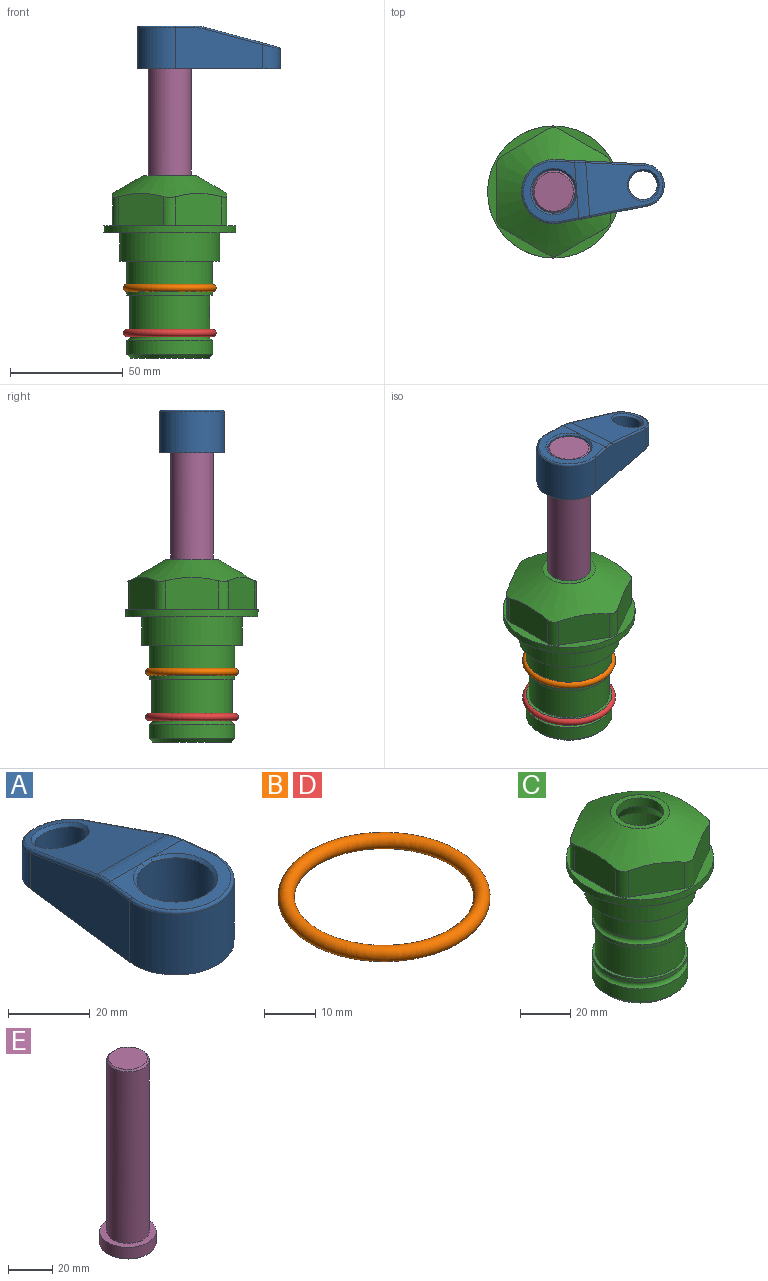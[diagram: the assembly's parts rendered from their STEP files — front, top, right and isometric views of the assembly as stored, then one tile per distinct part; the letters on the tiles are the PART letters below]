
ASSEMBLY  parts=5 mates=4
PART A: 31 faces, bbox 31.7x65.5x19.8 mm
  f0: plane 39.12x18.26mm, normal (0.99,0.12,0), area 612.2mm2, adj f1,f4,f7,f11,f13,f15
  f1: cylinder r=9.53mm len=18.91mm, axis (0,0,-1), area 296.1mm2, adj f0,f2,f7,f17
  f2: plane 39.12x18.26mm, normal (-0.99,0.12,0), area 612.2mm2, adj f1,f4,f7,f12,f14,f16
  f3: cylinder r=6.35mm len=12.7mm, axis (0,0,-1), area 362.4mm2, adj f7,f18
  f4: cylinder r=14.29mm len=28.58mm, axis (0,0,-1), area 882.2mm2, adj f0,f2,f7,f10
  f5: cylinder r=9.53mm len=19.05mm, axis (0,0,-1), area 1092.6mm2, adj f7,f19,f20
  f6: plane 26.99x23.69mm, normal (0,0,1), area 216.2mm2, adj f9,f10,f11,f12,f19
  f7: plane 63.5x28.58mm, normal (0,0,-1), area 661.8mm2, adj f0,f1,f2,f3,f4,f5,f22,f23
  f8: plane 33.52x23.6mm, normal (0,0.26,0.97), area 486mm2, adj f9,f15,f16,f17,f18
  f9: cylinder r=19.05mm len=24.72mm, axis (1,0,0), area 120.4mm2, adj f6,f8,f13,f14,f20
  f10: torus R=13.49mm, axis (0,0,1), area 59mm2, adj f4,f6,f11,f12
  f11: cylinder r=0.79mm len=8.67mm, axis (0.12,-0.99,0), area 10.8mm2, adj f0,f6,f10,f13
  f12: cylinder r=0.79mm len=8.67mm, axis (0.12,0.99,0), area 10.8mm2, adj f2,f6,f10,f14
  f13: bspline ~4.95x1.42mm, area 6.1mm2, adj f0,f9,f11,f15
  f14: bspline ~4.95x1.42mm, area 6.1mm2, adj f2,f9,f12,f16
  f15: cylinder r=0.79mm len=25.95mm, axis (0.12,-0.96,0.26), area 32.9mm2, adj f0,f8,f13,f17
  f16: cylinder r=0.79mm len=25.95mm, axis (0.12,0.96,-0.26), area 32.9mm2, adj f2,f8,f14,f17
  f17: bspline ~18.91x8.38mm, area 30mm2, adj f1,f8,f15,f16
  f18: bspline ~14.29x14.29mm, area 48.3mm2, adj f3,f8
  f19: cone r=9.53mm half-angle=45deg, axis (0,0,1), area 66.5mm2, adj f5,f6,f20
  f20: bspline ~3.22x0.96mm, area 3.5mm2, adj f5,f9,f19
  f21: plane 2.75x2.72mm, normal (0,0,-1), area 2.9mm2, adj f23,f25,f28
  f22: plane 23.05x15.88mm, normal (-0.99,-0.12,0), area 323.6mm2, adj f7,f25,f26,f27,f28,f29
  f23: plane 23.05x15.88mm, normal (0.99,-0.12,0), area 323.6mm2, adj f7,f21,f25,f27,f28,f30
  f24: cylinder r=9.53mm len=10.69mm, axis (0,0,-1), area 114.7mm2, adj f7,f27,f29,f30
  f25: cylinder r=12.7mm len=20.59mm, axis (0,0,-1), area 381.1mm2, adj f7,f21,f22,f23,f26,f28
  f26: plane 2.75x2.72mm, normal (0,0,-1), area 2.9mm2, adj f22,f25,f28
  f27: plane 19.72x18.37mm, normal (0,-0.26,-0.97), area 291.8mm2, adj f22,f23,f24,f28,f29,f30
  f28: cylinder r=15.88mm len=19.92mm, axis (1,0,0), area 54.8mm2, adj f21,f22,f23,f25,f26,f27
  f29: cylinder r=1.59mm len=11mm, axis (0,0,-1), area 34.7mm2, adj f7,f22,f24,f27
  f30: cylinder r=1.59mm len=11mm, axis (0,0,-1), area 34.7mm2, adj f7,f23,f24,f27
PART B: 1 faces, bbox 44.7x44.7x3.2 mm
  f0: torus R=19.05mm, axis (0,0,1), area 1193.9mm2
PART C: 36 faces, bbox 58.7x58.7x81 mm
  f0: cylinder r=17.78mm len=35.56mm, axis (0,0,1), area 1670.8mm2, adj f23,f24,f31
  f1: cylinder r=19.05mm len=38.1mm, axis (0,0,1), area 1191.9mm2, adj f26,f27,f30
  f2: plane 58.66x58.66mm, normal (0,0,-1), area 1150.6mm2, adj f3,f28
  f3: cylinder r=29.33mm len=58.66mm, axis (0,0,-1), area 585.1mm2, adj f2,f4
  f4: plane 58.66x58.66mm, normal (0,0,1), area 475.9mm2, adj f3,f5,f6,f7,f8,f9,f10,f11
  f5: plane 20.32x14.34mm, normal (-0.5,0.87,0), area 324.4mm2, adj f4,f15,f16,f17
  f6: plane 20.32x14.34mm, normal (0.5,0.87,0), area 324.4mm2, adj f4,f14,f15,f17
  f7: plane 23.48x14.34mm, normal (1,0,0), area 324.4mm2, adj f4,f13,f14,f17
  f8: plane 20.32x14.34mm, normal (0.5,-0.87,0), area 324.4mm2, adj f4,f12,f13,f17
  f9: plane 20.32x14.34mm, normal (-0.5,-0.87,0), area 324.4mm2, adj f4,f11,f12,f17
  f10: plane 23.48x14.34mm, normal (-1,0,0), area 324.4mm2, adj f4,f11,f16,f17
  f11: cylinder r=5.08mm len=12.85mm, axis (0,0,-1), area 67.2mm2, adj f4,f9,f10,f17
  f12: cylinder r=5.08mm len=12.85mm, axis (0,0,-1), area 67.2mm2, adj f4,f8,f9,f17
  f13: cylinder r=5.08mm len=12.85mm, axis (0,0,-1), area 67.2mm2, adj f4,f7,f8,f17
  f14: cylinder r=5.08mm len=12.85mm, axis (0,0,-1), area 67.2mm2, adj f4,f6,f7,f17
  f15: cylinder r=5.08mm len=12.85mm, axis (0,0,-1), area 67.2mm2, adj f4,f5,f6,f17
  f16: cylinder r=5.08mm len=12.85mm, axis (0,0,-1), area 67.2mm2, adj f4,f5,f10,f17
  f17: cone r=11.73mm half-angle=60deg, axis (0,0,-1), area 2071.8mm2, adj f5,f6,f7,f8,f9,f10,f11,f12
  f18: plane 23.46x23.46mm, normal (0,0,1), area 147.4mm2, adj f17,f35
  f19: plane 34.93x34.93mm, normal (0,0,-1), area 958mm2, adj f29
  f20: cylinder r=19.05mm len=38.1mm, axis (0,0,1), area 760.1mm2, adj f21,f29
  f21: torus R=19.05mm, axis (0,0,1), area 565.3mm2, adj f20,f22
  f22: cylinder r=19.05mm len=38.1mm, axis (0,0,1), area 190mm2, adj f21,f23
  f23: plane 38.1x38.1mm, normal (0,0,1), area 146.9mm2, adj f0,f22
  f24: plane 38.1x38.1mm, normal (0,0,-1), area 146.9mm2, adj f0,f25
  f25: cylinder r=19.05mm len=38.1mm, axis (0,0,1), area 190mm2, adj f24,f26
  f26: torus R=19.05mm, axis (0,0,1), area 565.3mm2, adj f1,f25
  f27: plane 44.45x44.45mm, normal (0,0,-1), area 411.7mm2, adj f1,f28
  f28: cylinder r=22.23mm len=44.45mm, axis (0,0,1), area 1773.5mm2, adj f2,f27
  f29: cone r=19.05mm half-angle=45deg, axis (0,0,1), area 257.5mm2, adj f19,f20
  f30: cylinder r=3.17mm len=6.75mm, axis (-1,0,0), area 128mm2, adj f1,f33
  f31: cylinder r=3.17mm len=6.35mm, axis (-1,0,0), area 102.5mm2, adj f0,f33
  f32: plane 25.4x25.4mm, normal (0,0,1), area 506.7mm2, adj f33
  f33: cylinder r=12.7mm len=66.42mm, axis (0,0,-1), area 5236.2mm2, adj f30,f31,f32,f34
  f34: cone r=9.53mm half-angle=30deg, axis (0,0,-1), area 443.4mm2, adj f33,f35
  f35: cylinder r=9.53mm len=19.05mm, axis (0,0,-1), area 240.9mm2, adj f18,f34
PART D: same geometry as B
PART E: 6 faces, bbox 25.4x25.4x101.6 mm
  f0: plane 17.46x17.46mm, normal (0,0,1), area 239.5mm2, adj f5
  f1: plane 25.4x25.4mm, normal (0,0,-1), area 506.7mm2, adj f2
  f2: cylinder r=12.7mm len=25.4mm, axis (0,0,1), area 506.7mm2, adj f1,f3
  f3: plane 25.4x25.4mm, normal (0,0,1), area 221.7mm2, adj f2,f4
  f4: cylinder r=9.53mm len=94.46mm, axis (0,0,1), area 5653mm2, adj f3,f5
  f5: cone r=8.73mm half-angle=45deg, axis (0,0,-1), area 64.4mm2, adj f0,f4
PLACE A rot(axis=(0,0,-1),85.9deg) t=(0,0,28.35)mm
PLACE B at identity
PLACE C at identity fixed
PLACE D t=(0,0,-20)mm
PLACE E rot(axis=(0,0,-1),85.9deg) t=(0,0,27.55)mm
MATE fastened B.f0 <-> C.f0  axis (0,0,1) through (0,0,-24.51)mm
MATE fastened D.f0 <-> C.f0  axis (0,0,1) through (0,0,-44.51)mm
MATE cylindrical E.f2 <-> C.f0  axis (0,0,-1) through (0,0,-10.55)mm
MATE fastened E.f2 <-> A.f4  axis (0,0,1) through (0,0,91.05)mm
